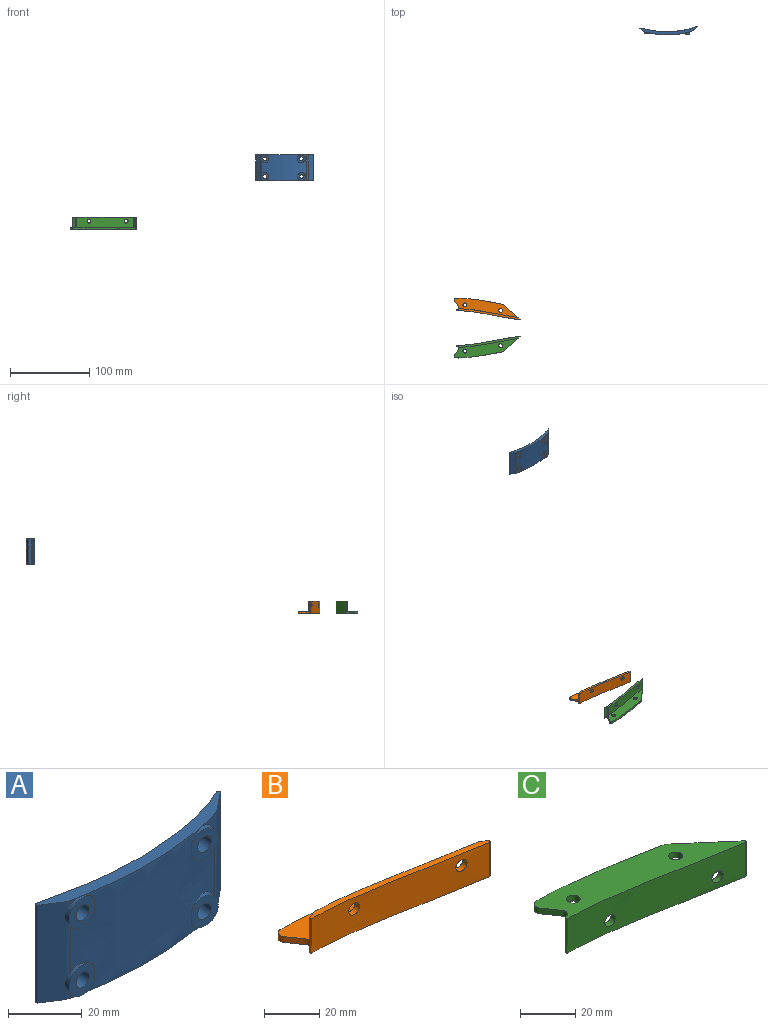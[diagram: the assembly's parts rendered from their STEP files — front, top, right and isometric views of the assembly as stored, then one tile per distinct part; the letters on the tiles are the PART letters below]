
ASSEMBLY  parts=3 mates=1
PART A: 23 faces, bbox 73.1x11.1x32.5 mm
  f0: plane 73.05x11.09mm, normal (0,0,1), area 260.3mm2, adj f1,f2,f3,f4,f18,f19,f20,f22
  f1: extruded ~71.7x32.51mm, area 2296.8mm2, adj f0,f5,f10,f11,f16,f17,f20,f21
  f2: plane 32.51x6.51mm, normal (0.63,-0.78,0), area 271.7mm2, adj f0,f5,f19,f20,f21
  f3: extruded ~56.65x32.51mm, area 1556.6mm2, adj f0,f5,f6,f7,f8,f9,f12,f13
  f4: plane 32.51x6mm, normal (-0.54,-0.84,0), area 232.7mm2, adj f0,f5,f18,f22
  f5: plane 73.05x11.09mm, normal (0,0,-1), area 260.3mm2, adj f1,f2,f3,f4,f18,f19,f21,f22
  f6: cylinder r=5.03mm len=10.06mm, axis (0.02,1,0), area 23.9mm2, adj f3,f7,f18
  f7: plane 10.06x9.37mm, normal (-0.02,-1,0), area 57.7mm2, adj f3,f6,f11
  f8: cylinder r=5.03mm len=10.06mm, axis (0.02,1,0), area 23.9mm2, adj f3,f9,f18
  f9: plane 10.06x9.37mm, normal (-0.02,-1,0), area 57.7mm2, adj f3,f8,f10
  f10: cylinder r=2.49mm len=5.1mm, axis (0.02,1,0), area 70.6mm2, adj f1,f9
  f11: cylinder r=2.49mm len=5.1mm, axis (0.02,1,0), area 70.6mm2, adj f1,f7
  f12: plane 10.06x9.63mm, normal (-0.07,-1,0), area 58.9mm2, adj f3,f13,f17
  f13: cylinder r=5.03mm len=10.06mm, axis (0.07,1,0), area 41.1mm2, adj f3,f12
  f14: plane 10.06x9.63mm, normal (-0.07,-1,0), area 58.9mm2, adj f3,f15,f16
  f15: cylinder r=5.03mm len=10.06mm, axis (0.07,1,0), area 41.1mm2, adj f3,f14
  f16: cylinder r=2.49mm len=6.34mm, axis (0.07,1,0), area 81.5mm2, adj f1,f14
  f17: cylinder r=2.49mm len=6.34mm, axis (0.07,1,0), area 81.5mm2, adj f1,f12
  f18: cylinder r=5.08mm len=32.51mm, axis (0,0,-1), area 46mm2, adj f0,f3,f4,f5,f6,f8
  f19: cylinder r=5.08mm len=32.51mm, axis (0,0,-1), area 63.8mm2, adj f0,f2,f3,f5
  f20: cylinder r=0.51mm len=16.26mm, axis (0,0,-1), area 24mm2, adj f0,f1,f2,f21
  f21: cylinder r=0.51mm len=16.26mm, axis (0,0,-1), area 24mm2, adj f1,f2,f5,f20
  f22: cylinder r=0.51mm len=32.51mm, axis (0,0,-1), area 46.2mm2, adj f0,f1,f4,f5
PART B: 20 faces, bbox 83.9x28.5x16.2 mm
  f0: plane 83.66x28.31mm, normal (0,0,-1), area 1082.3mm2, adj f1,f2,f3,f5,f7,f9,f10,f13
  f1: plane 20.88x17.98mm, normal (0.65,0.76,0), area 99.2mm2, adj f0,f4,f8,f15,f17,f19
  f2: extruded ~57.01x7.55mm, area 146.3mm2, adj f0,f4,f13,f19
  f3: plane 6.67x4.63mm, normal (-0.82,-0.57,0), area 20.6mm2, adj f0,f4,f13,f14
  f4: plane 81.94x26.11mm, normal (0,0,1), area 878.8mm2, adj f1,f2,f3,f6,f7,f9,f10,f13
  f5: extruded ~79.38x15.24mm, area 1185.2mm2, adj f0,f8,f11,f12,f17,f18
  f6: extruded ~72.27x12.7mm, area 893.9mm2, adj f4,f8,f11,f12,f15,f16
  f7: plane 15.24x3.72mm, normal (-0.34,0.94,0), area 53mm2, adj f0,f4,f8,f14,f16,f18
  f8: plane 81.05x14.72mm, normal (0,0,1), area 200.4mm2, adj f1,f5,f6,f7,f15,f16,f17,f18
  f9: cylinder r=2.49mm len=4.98mm, axis (0,0,-1), area 39.7mm2, adj f0,f4
  f10: cylinder r=2.49mm len=4.98mm, axis (0,0,-1), area 39.7mm2, adj f0,f4
  f11: cylinder r=2.49mm len=5.33mm, axis (0.17,0.99,0), area 39.7mm2, adj f5,f6
  f12: cylinder r=2.49mm len=5.25mm, axis (0.12,0.99,0), area 39.7mm2, adj f5,f6
  f13: cylinder r=2.54mm len=3.99mm, axis (0,0,-1), area 13.9mm2, adj f0,f2,f3,f4
  f14: cylinder r=2.54mm len=3.84mm, axis (0,0,-1), area 11.8mm2, adj f0,f3,f4,f7
  f15: cylinder r=2.54mm len=12.7mm, axis (0,0,-1), area 17.9mm2, adj f1,f4,f6,f8
  f16: cylinder r=2.54mm len=12.7mm, axis (0,0,-1), area 12.7mm2, adj f4,f6,f7,f8
  f17: cylinder r=0.51mm len=15.24mm, axis (0,0,-1), area 20mm2, adj f0,f1,f5,f8
  f18: cylinder r=0.51mm len=15.24mm, axis (0,0,-1), area 21.9mm2, adj f0,f5,f7,f8
  f19: cylinder r=5.08mm len=2.54mm, axis (0,0,-1), area 6.8mm2, adj f0,f1,f2,f4
PART C: 20 faces, bbox 83.9x28.5x16.2 mm
  f0: plane 83.66x28.31mm, normal (0,0,1), area 1082.3mm2, adj f1,f2,f3,f5,f7,f9,f10,f13
  f1: plane 20.88x17.98mm, normal (0.65,0.76,0), area 99.2mm2, adj f0,f4,f8,f15,f17,f19
  f2: extruded ~57.01x7.55mm, area 146.3mm2, adj f0,f4,f13,f19
  f3: plane 6.67x4.63mm, normal (-0.82,-0.57,0), area 20.6mm2, adj f0,f4,f13,f14
  f4: plane 81.94x26.11mm, normal (0,0,-1), area 878.8mm2, adj f1,f2,f3,f6,f7,f9,f10,f13
  f5: extruded ~79.38x15.24mm, area 1185.2mm2, adj f0,f8,f11,f12,f17,f18
  f6: extruded ~72.27x12.7mm, area 893.9mm2, adj f4,f8,f11,f12,f15,f16
  f7: plane 15.24x3.72mm, normal (-0.34,0.94,0), area 53mm2, adj f0,f4,f8,f14,f16,f18
  f8: plane 81.05x14.7mm, normal (0,0,-1), area 200.4mm2, adj f1,f5,f6,f7,f15,f16,f17,f18
  f9: cylinder r=2.49mm len=4.98mm, axis (0,0,1), area 39.7mm2, adj f0,f4
  f10: cylinder r=2.49mm len=4.98mm, axis (0,0,1), area 39.7mm2, adj f0,f4
  f11: cylinder r=2.49mm len=5.34mm, axis (0.17,0.99,0), area 39.6mm2, adj f5,f6
  f12: cylinder r=2.49mm len=5.25mm, axis (0.12,0.99,0), area 39.7mm2, adj f5,f6
  f13: cylinder r=2.54mm len=3.99mm, axis (0,0,1), area 13.9mm2, adj f0,f2,f3,f4
  f14: cylinder r=2.54mm len=3.84mm, axis (0,0,1), area 11.8mm2, adj f0,f3,f4,f7
  f15: cylinder r=2.54mm len=12.7mm, axis (0,0,1), area 17.9mm2, adj f1,f4,f6,f8
  f16: cylinder r=2.54mm len=12.7mm, axis (0,0,1), area 12.7mm2, adj f4,f6,f7,f8
  f17: cylinder r=0.51mm len=15.24mm, axis (0,0,1), area 20mm2, adj f0,f1,f5,f8
  f18: cylinder r=0.51mm len=15.24mm, axis (0,0,1), area 21.9mm2, adj f0,f5,f7,f8
  f19: cylinder r=5.08mm len=2.54mm, axis (0,0,1), area 6.8mm2, adj f0,f1,f2,f4
PLACE A t=(120.71,86.24,77.62)mm
PLACE B t=(16.29,26.82,0)mm
PLACE C rot(axis=(1,0,0),180deg) t=(16.28,23.98,0)mm
MATE fastened B.f0 <-> C.f0  axis (0,0,-1) through (0,50.8,0)mm
